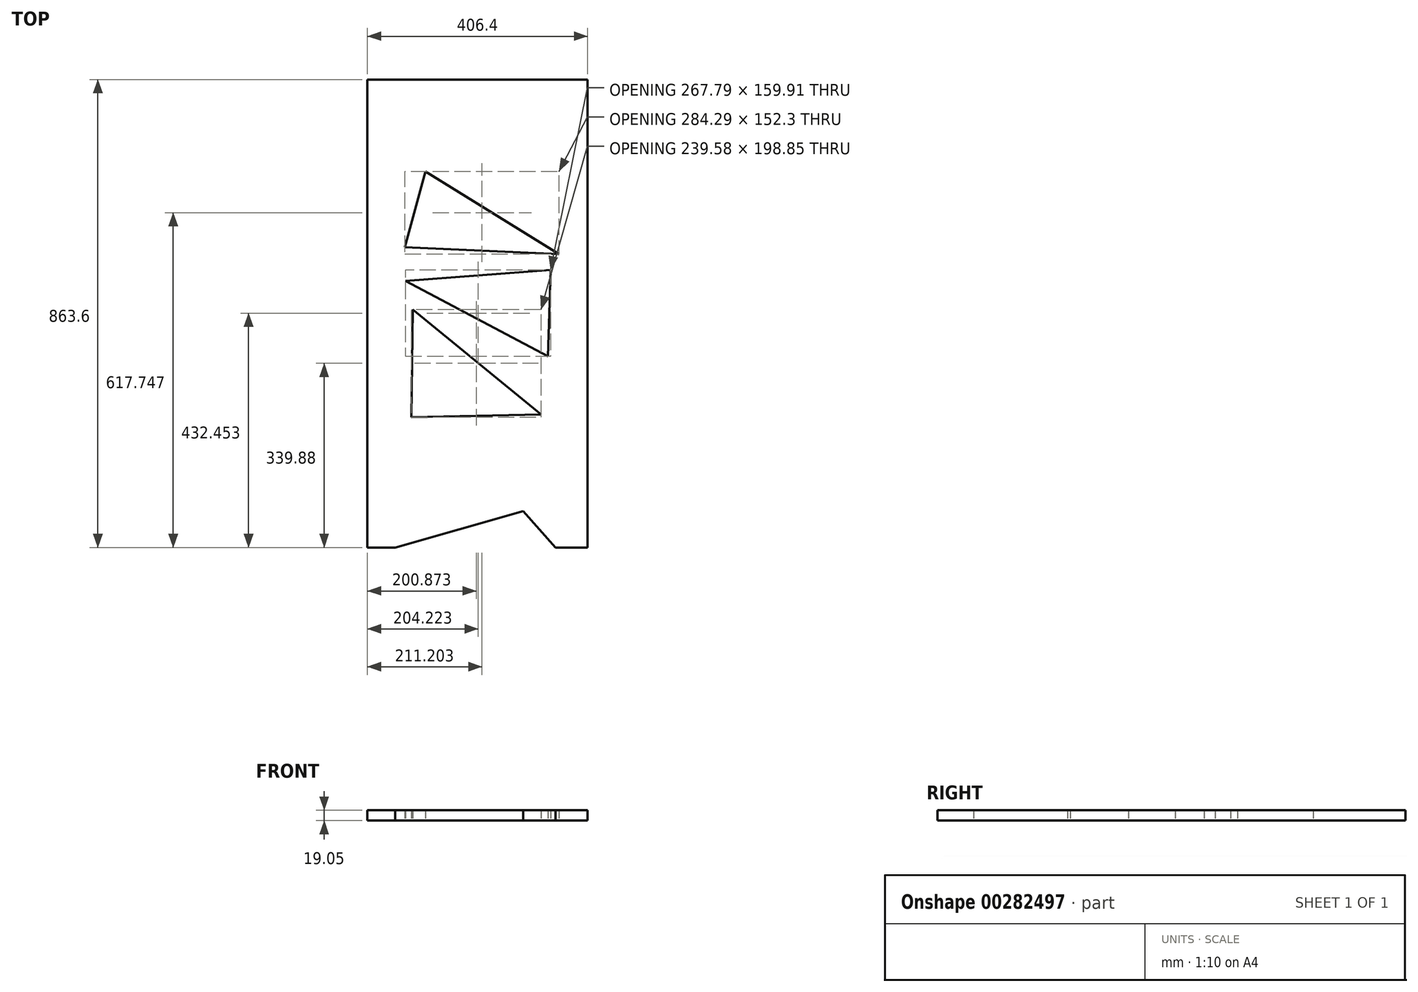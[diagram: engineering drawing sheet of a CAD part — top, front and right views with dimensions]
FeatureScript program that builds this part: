
annotation { "Feature Type Name" : "Feature", "Feature Type Description" : "" }
export const myFeature = defineFeature(function(context is Context, id is Id, definition is map)
    precondition{}
    {
        {
            var Q0;
            Q0=qCreatedBy(makeId("Top.planeOp"),FACE);
            var sketch = newSketch(context, id + "F0", { "sketchPlane" : qUnion([Q0])});
            skLineSegment(sketch, "E0", {"start": v(-348.89, -1.53) * mm, "end": v(-349.19, -1.5) * mm});
            skLineSegment(sketch, "E1.bottom", {"start": v(-109.35, 397.32) * mm, "end": v(297.05, 397.32) * mm});
            skLineSegment(sketch, "E1.top", {"start": v(-109.35, -466.28) * mm, "end": v(-58.06, -466.28) * mm});
            skLineSegment(sketch, "E1.left", {"start": v(-109.35, 397.32) * mm, "end": v(-109.35, -466.28) * mm});
            skLineSegment(sketch, "E1.right", {"start": v(297.05, 397.32) * mm, "end": v(297.05, -466.28) * mm});
            skLineSegment(sketch, "E2", {"start": v(-58.06, -466.28) * mm, "end": v(178, -399.34) * mm});
            skLineSegment(sketch, "E3", {"start": v(178, -399.34) * mm, "end": v(237.65, -466.28) * mm});
            skLineSegment(sketch, "E4.trimOffspring", {"start": v(237.65, -466.28) * mm, "end": v(297.05, -466.28) * mm});
            skLineSegment(sketch, "E5", {"start": v(93.85, 397.32) * mm, "end": v(93.85, 270.32) * mm, "construction": true});
            skLineSegment(sketch, "E6", {"start": v(244, 75.32) * mm, "end": v(-40.29, 88.01) * mm});
            skLineSegment(sketch, "E7", {"start": v(-40.29, 88.01) * mm, "end": v(-2.22, 227.62) * mm});
            skLineSegment(sketch, "E8", {"start": v(223.7, -113.78) * mm, "end": v(-39.02, 25.82) * mm});
            skLineSegment(sketch, "E9", {"start": v(-39.02, 25.82) * mm, "end": v(228.77, 46.13) * mm});
            skLineSegment(sketch, "E10", {"start": v(-25.87, -26.97) * mm, "end": v(-28.27, -225.83) * mm});
            skLineSegment(sketch, "E11", {"start": v(-28.27, -225.83) * mm, "end": v(211.31, -221.03) * mm});
            skLineSegment(sketch, "E12", {"start": v(228.77, 46.13) * mm, "end": v(223.7, -113.78) * mm});
            skLineSegment(sketch, "E13", {"start": v(-2.22, 227.62) * mm, "end": v(244, 75.32) * mm});
            skLineSegment(sketch, "E14", {"start": v(-25.87, -26.97) * mm, "end": v(211.31, -221.03) * mm});
            skSolve(sketch);
        }
        {
            var Q0;
            Q0 = qSketchRegion(id + "F0", true);
            extrude(context, id + "F1", {"entities" : qUnion([Q0]), "depth" : 19.05 * mm});
        }
    });
